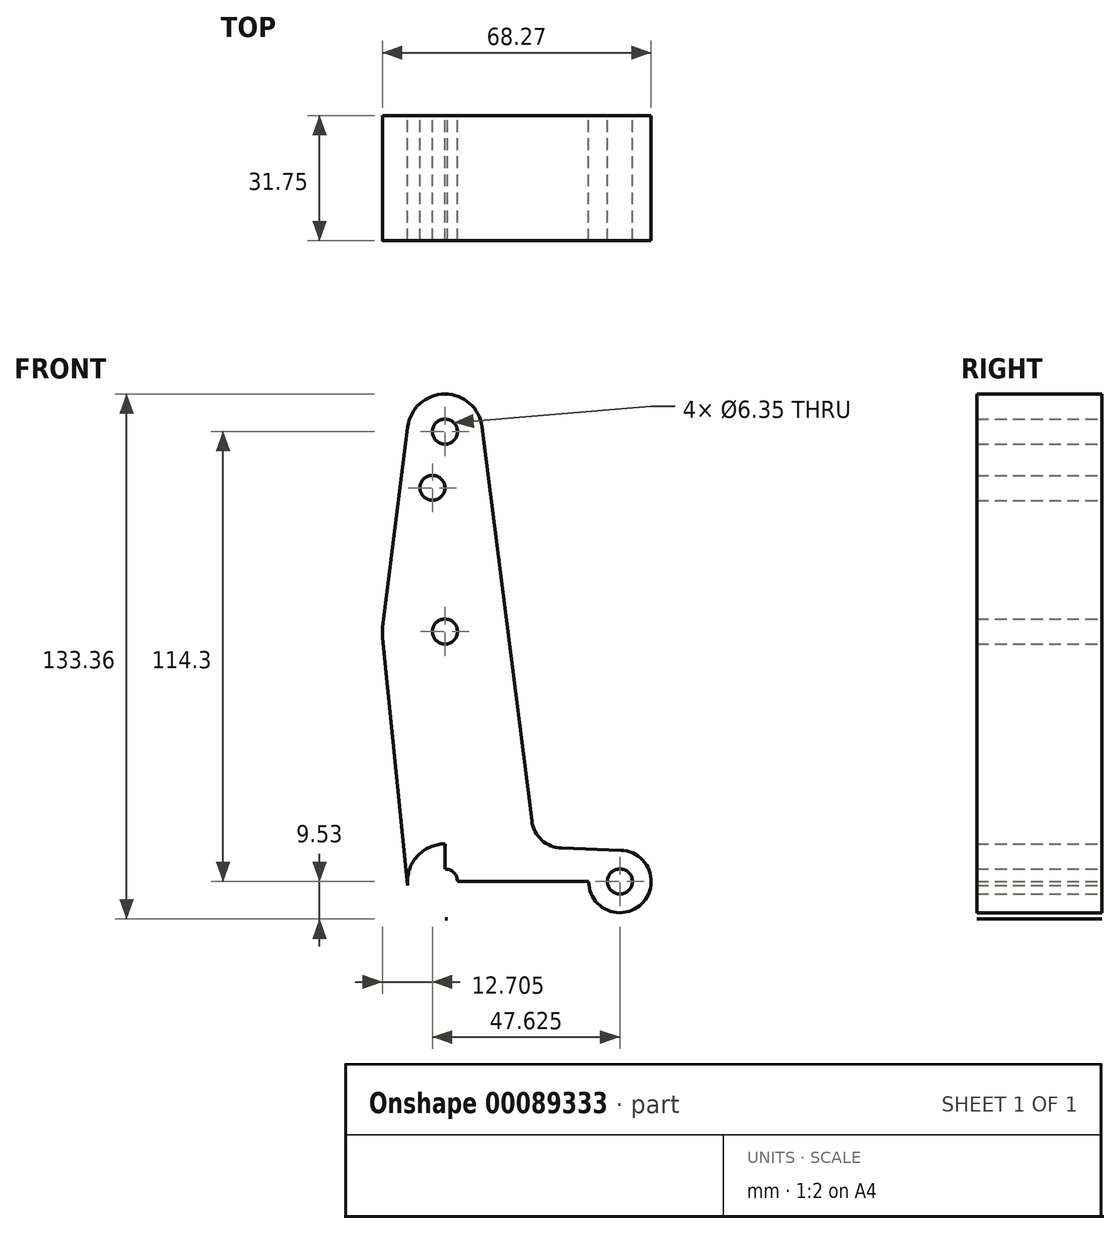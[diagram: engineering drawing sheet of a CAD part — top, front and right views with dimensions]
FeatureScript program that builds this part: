
annotation { "Feature Type Name" : "Feature", "Feature Type Description" : "" }
export const myFeature = defineFeature(function(context is Context, id is Id, definition is map)
    precondition{}
    {
        {
            var Q0;
            Q0=qCreatedBy(makeId("Front.planeOp"),FACE);
            var sketch = newSketch(context, id + "F0", { "sketchPlane" : qUnion([Q0])});
            skCircle(sketch, "E0", {"center": v(0, 114.3) * mm, "radius": 9.53 * mm});
            skCircle(sketch, "E1", {"center": v(0, 63.5) * mm, "radius": 15.88 * mm});
            skCircle(sketch, "E2", {"center": v(0, 0) * mm, "radius": 9.53 * mm});
            skCircle(sketch, "E3", {"center": v(44.45, 0) * mm, "radius": 7.94 * mm});
            skLineSegment(sketch, "E4", {"start": v(0, 114.3) * mm, "end": v(0, 0) * mm});
            skLineSegment(sketch, "E5", {"start": v(0, 0) * mm, "end": v(44.45, 0) * mm});
            skLineSegment(sketch, "E6", {"start": v(9.45, 115.5) * mm, "end": v(15.75, 65.48) * mm});
            skLineSegment(sketch, "E7", {"start": v(-9.45, 115.5) * mm, "end": v(-15.75, 65.48) * mm});
            skLineSegment(sketch, "E8", {"start": v(15.75, 65.48) * mm, "end": v(22.06, 15.42) * mm});
            skLineSegment(sketch, "E9", {"start": v(0, -9.53) * mm, "end": v(44.73, -7.93) * mm});
            skCircle(sketch, "E10", {"center": v(0, 63.5) * mm, "radius": 0.32 * mm});
            skCircle(sketch, "E11", {"center": v(0, 0) * mm, "radius": 0.32 * mm});
            skCircle(sketch, "E12", {"center": v(44.45, 0) * mm, "radius": 0.32 * mm});
            skCircle(sketch, "E13", {"center": v(0, 114.3) * mm, "radius": 0.32 * mm});
            skCircle(sketch, "E14", {"center": v(-3.18, 100.03) * mm, "radius": 3.18 * mm});
            skCircle(sketch, "E15", {"center": v(0, 114.3) * mm, "radius": 3.18 * mm});
            skCircle(sketch, "E16", {"center": v(0, 63.5) * mm, "radius": 3.18 * mm});
            skCircle(sketch, "E17", {"center": v(0, 0) * mm, "radius": 3.18 * mm});
            skCircle(sketch, "E18", {"center": v(44.45, 0) * mm, "radius": 3.18 * mm});
            skLineSegment(sketch, "E19", {"start": v(29.66, 8.47) * mm, "end": v(44.73, 7.93) * mm});
            skArc(sketch, "E20.filletArc", {"start": v(22.06, 15.42) * mm, "mid": v(24.58, 10.55) * mm, "end": v(29.66, 8.47) * mm});
            skLineSegment(sketch, "E21", {"start": v(-15.8, 61.91) * mm, "end": v(-9.48, -0.95) * mm});
            skSolve(sketch);
        }
        {
            var Q0;
            {var subQ8=sQuery(id+"F0.wireOp",EDGE,"E8");Q0=makeQuery(id+"F0.imprint","IMPRINT",FACE,{"disambiguationData":[TD([[makeQuery(id+"F0.imprint","IMPRINT",EDGE,{"derivedFrom":subQ8}),-1.0]])]});}
            var Q1;
            {var subQ0=sQuery(id+"F0.wireOp",EDGE,"E4");var subQ1=sQuery(id+"F0.wireOp",EDGE,"E1");var subQ6=makeQuery(id+"F0.imprint","INTERSECT",VERTEX,{"disambiguationData":[OD(1.0)],"derivedFrom":[subQ1,subQ0]});Q1=makeQuery(id+"F0.imprint","IMPRINT",FACE,{"disambiguationData":[TD([[makeQuery(id+"F0.imprint","IMPRINT",EDGE,{"disambiguationData":[TD([[subQ6,-1.0]])],"derivedFrom":subQ0}),1.0]])]});}
            var Q2;
            {var subQ1=sQuery(id+"F0.wireOp",EDGE,"E1");var subQ5=makeQuery(id+"F0.imprint","IMPRINT",VERTEX,{"derivedFrom":subQ1});Q2=makeQuery(id+"F0.imprint","IMPRINT",FACE,{"disambiguationData":[TD([[makeQuery(id+"F0.imprint","IMPRINT",EDGE,{"disambiguationData":[TD([[subQ5,1.0]])],"derivedFrom":subQ1}),1.0]])]});}
            var Q3;
            {var subQ6=sQuery(id+"F0.wireOp",EDGE,"E6");Q3=makeQuery(id+"F0.imprint","IMPRINT",FACE,{"disambiguationData":[TD([[makeQuery(id+"F0.imprint","IMPRINT",EDGE,{"derivedFrom":subQ6}),-1.0]])]});}
            var Q4;
            {var subQ5=sQuery(id+"F0.wireOp",EDGE,"E7");Q4=makeQuery(id+"F0.imprint","IMPRINT",FACE,{"disambiguationData":[TD([[makeQuery(id+"F0.imprint","IMPRINT",EDGE,{"derivedFrom":subQ5}),1.0]])]});}
            var Q5;
            Q5=makeQuery(id+"F0.imprint","IMPRINT",FACE,{"disambiguationData":[TD([[makeQuery(id+"F0.imprint","IMPRINT",EDGE,{"derivedFrom":sQuery(id+"F0.wireOp",EDGE,"E15")}),-1.0]])]});
            var Q6;
            Q6=makeQuery(id+"F0.imprint","IMPRINT",FACE,{"disambiguationData":[TD([[makeQuery(id+"F0.imprint","IMPRINT",EDGE,{"derivedFrom":sQuery(id+"F0.wireOp",EDGE,"E15")}),-1.0]])]});
            var Q7;
            {var subQ0=sQuery(id+"F0.wireOp",EDGE,"E9");var subQ1=sQuery(id+"F0.wireOp",EDGE,"E2");var subQ2=makeQuery(id+"F0.imprint","INTERSECT",VERTEX,{"disambiguationData":[OD(1.0)],"derivedFrom":[subQ1,subQ0]});Q7=makeQuery(id+"F0.imprint","IMPRINT",FACE,{"disambiguationData":[TD([[makeQuery(id+"F0.imprint","IMPRINT",EDGE,{"disambiguationData":[TD([[subQ2,-1.0]])],"derivedFrom":subQ1}),-1.0]])]});}
            var Q8;
            {var subQ1=sQuery(id+"F0.wireOp",EDGE,"E2");var subQ8=sQuery(id+"F0.wireOp",EDGE,"E9");var subQ9=makeQuery(id+"F0.imprint","INTERSECT",VERTEX,{"disambiguationData":[OD(0.0)],"derivedFrom":[subQ1,subQ8]});Q8=makeQuery(id+"F0.imprint","IMPRINT",FACE,{"disambiguationData":[TD([[makeQuery(id+"F0.imprint","IMPRINT",EDGE,{"disambiguationData":[TD([[subQ9,1.0]])],"derivedFrom":subQ1}),1.0]])]});}
            var Q9;
            {var subQ0=sQuery(id+"F0.wireOp",EDGE,"E4");var subQ1=sQuery(id+"F0.wireOp",EDGE,"E2");var subQ2=makeQuery(id+"F0.imprint","INTERSECT",VERTEX,{"derivedFrom":[subQ1,subQ0]});Q9=makeQuery(id+"F0.imprint","IMPRINT",FACE,{"disambiguationData":[TD([[makeQuery(id+"F0.imprint","IMPRINT",EDGE,{"disambiguationData":[TD([[subQ2,1.0]])],"derivedFrom":subQ1}),1.0]])]});}
            var Q10;
            Q10=makeQuery(id+"F0.imprint","IMPRINT",FACE,{"disambiguationData":[TD([[makeQuery(id+"F0.imprint","IMPRINT",EDGE,{"derivedFrom":sQuery(id+"F0.wireOp",EDGE,"E18")}),-1.0]])]});
            var Q11;
            {var subQ1=sQuery(id+"F0.wireOp",EDGE,"E1");var subQ8=makeQuery(id+"F0.imprint","INTERSECT",VERTEX,{"derivedFrom":[subQ1,sQuery(id+"F0.wireOp",EDGE,"E7")]});Q11=makeQuery(id+"F0.imprint","IMPRINT",FACE,{"disambiguationData":[TD([[makeQuery(id+"F0.imprint","IMPRINT",EDGE,{"disambiguationData":[TD([[subQ8,1.0]])],"derivedFrom":subQ1}),1.0]])]});}
            var Q12;
            {var subQ0=sQuery(id+"F0.wireOp",EDGE,"E4");var subQ1=sQuery(id+"F0.wireOp",EDGE,"E1");var subQ6=makeQuery(id+"F0.imprint","INTERSECT",VERTEX,{"disambiguationData":[OD(0.0)],"derivedFrom":[subQ1,subQ0]});Q12=makeQuery(id+"F0.imprint","IMPRINT",FACE,{"disambiguationData":[TD([[makeQuery(id+"F0.imprint","IMPRINT",EDGE,{"disambiguationData":[TD([[subQ6,-1.0]])],"derivedFrom":subQ0}),1.0]])]});}
            var Q13;
            {var subQ0=sQuery(id+"F0.wireOp",EDGE,"E21");Q13=makeQuery(id+"F0.imprint","IMPRINT",FACE,{"disambiguationData":[TD([[makeQuery(id+"F0.imprint","IMPRINT",EDGE,{"derivedFrom":subQ0}),1.0]])]});}
            extrude(context, id + "F1", {"entities" : qUnion([Q0, Q1, Q2, Q3, Q4, Q5, Q6, Q7, Q8, Q9, Q10, Q11, Q12, Q13]), "depth" : 31.75 * mm});
        }
    });
